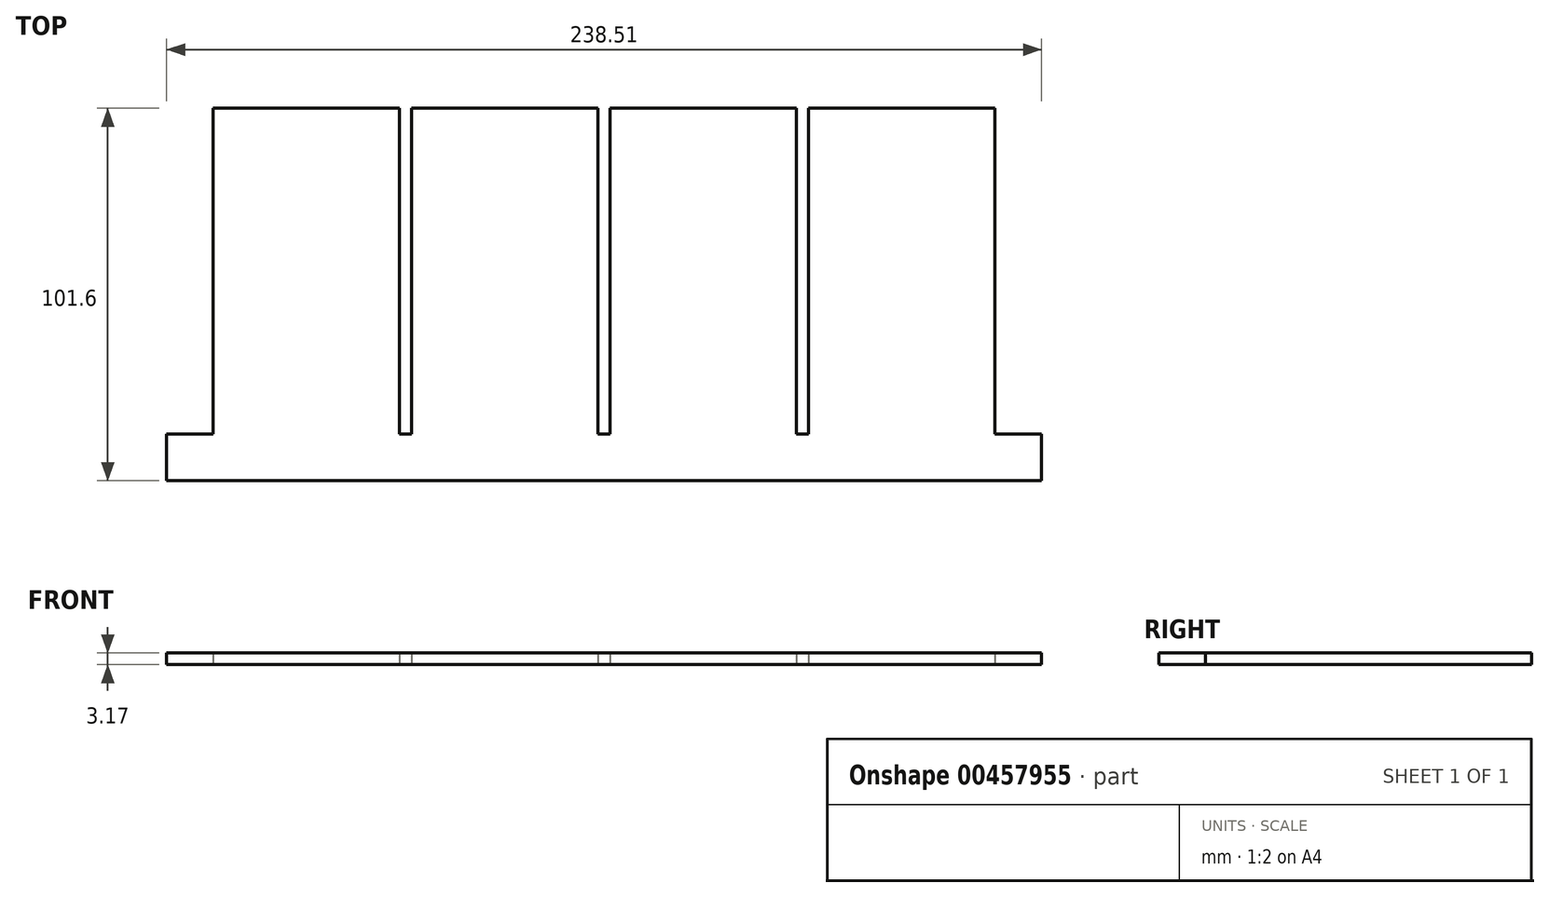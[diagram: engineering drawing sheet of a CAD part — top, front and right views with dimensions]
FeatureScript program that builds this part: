
annotation { "Feature Type Name" : "Feature", "Feature Type Description" : "" }
export const myFeature = defineFeature(function(context is Context, id is Id, definition is map)
    precondition{}
    {
        {
            var Q0;
            Q0=qCreatedBy(makeId("Top.planeOp"),FACE);
            var sketch = newSketch(context, id + "F0", { "sketchPlane" : qUnion([Q0])});
            skLineSegment(sketch, "E0", {"start": v(0, 0) * mm, "end": v(213.1, 0) * mm});
            skLineSegment(sketch, "E1", {"start": v(213.1, 12.7) * mm, "end": v(213.1, 101.6) * mm});
            skLineSegment(sketch, "E2", {"start": v(213.1, 101.6) * mm, "end": v(162.3, 101.6) * mm});
            skLineSegment(sketch, "E3", {"start": v(162.3, 101.6) * mm, "end": v(162.3, 12.7) * mm});
            skLineSegment(sketch, "E4", {"start": v(159, 12.7) * mm, "end": v(159, 101.6) * mm});
            skLineSegment(sketch, "E5", {"start": v(159, 101.6) * mm, "end": v(108.2, 101.6) * mm});
            skLineSegment(sketch, "E6", {"start": v(108.2, 101.6) * mm, "end": v(108.2, 12.7) * mm});
            skLineSegment(sketch, "E7", {"start": v(104.9, 12.7) * mm, "end": v(104.9, 101.6) * mm});
            skLineSegment(sketch, "E8", {"start": v(104.9, 101.6) * mm, "end": v(54.1, 101.6) * mm});
            skLineSegment(sketch, "E9", {"start": v(54.1, 101.6) * mm, "end": v(54.1, 12.7) * mm});
            skLineSegment(sketch, "E10", {"start": v(50.8, 12.7) * mm, "end": v(50.8, 101.6) * mm});
            skLineSegment(sketch, "E11", {"start": v(50.8, 101.6) * mm, "end": v(0, 101.6) * mm});
            skLineSegment(sketch, "E12", {"start": v(0, 101.6) * mm, "end": v(0, 12.7) * mm});
            skLineSegment(sketch, "E13", {"start": v(104.9, 12.7) * mm, "end": v(108.2, 12.7) * mm});
            skLineSegment(sketch, "E14", {"start": v(159, 12.7) * mm, "end": v(162.3, 12.7) * mm});
            skLineSegment(sketch, "E15", {"start": v(50.8, 12.7) * mm, "end": v(54.1, 12.7) * mm});
            skPoint(sketch, "E16.orphan", {"position": v(162.3, 0) * mm});
            skPoint(sketch, "E17.start.orphan", {"position": v(162.1, 0) * mm});
            skPoint(sketch, "E18.start.orphan", {"position": v(108.2, 0) * mm});
            skPoint(sketch, "E19.start.orphan", {"position": v(54.1, 0) * mm});
            skLineSegment(sketch, "E20.bottom", {"start": v(0, 0) * mm, "end": v(-12.7, 0) * mm});
            skLineSegment(sketch, "E20.top", {"start": v(0, 12.7) * mm, "end": v(-12.7, 12.7) * mm});
            skLineSegment(sketch, "E20.right", {"start": v(-12.7, 0) * mm, "end": v(-12.7, 12.7) * mm});
            skLineSegment(sketch, "E21.bottom", {"start": v(213.1, 0) * mm, "end": v(225.8, 0) * mm});
            skLineSegment(sketch, "E21.top", {"start": v(213.1, 12.7) * mm, "end": v(225.8, 12.7) * mm});
            skLineSegment(sketch, "E21.right", {"start": v(225.8, 0) * mm, "end": v(225.8, 12.7) * mm});
            skSolve(sketch);
        }
        {
            var Q0;
            Q0=makeQuery(id+"F0.imprint","IMPRINT",FACE,{"disambiguationData":[TD([[makeQuery(id+"F0.imprint","IMPRINT",EDGE,{"derivedFrom":sQuery(id+"F0.wireOp",EDGE,"E0")}),1.0]])]});
            var Q1;
            Q1=makeQuery(id+"F0.imprint","IMPRINT",FACE,{"disambiguationData":[TD([[makeQuery(id+"F0.imprint","IMPRINT",EDGE,{"derivedFrom":sQuery(id+"F0.wireOp",EDGE,"E21.bottom")}),1.0]])]});
            var Q2;
            Q2=makeQuery(id+"F0.imprint","IMPRINT",FACE,{"disambiguationData":[TD([[makeQuery(id+"F0.imprint","IMPRINT",EDGE,{"derivedFrom":sQuery(id+"F0.wireOp",EDGE,"E20.bottom")}),-1.0]])]});
            extrude(context, id + "F1", {"entities" : qUnion([Q0, Q1, Q2]), "depth" : 3.17 * mm});
        }
    });
